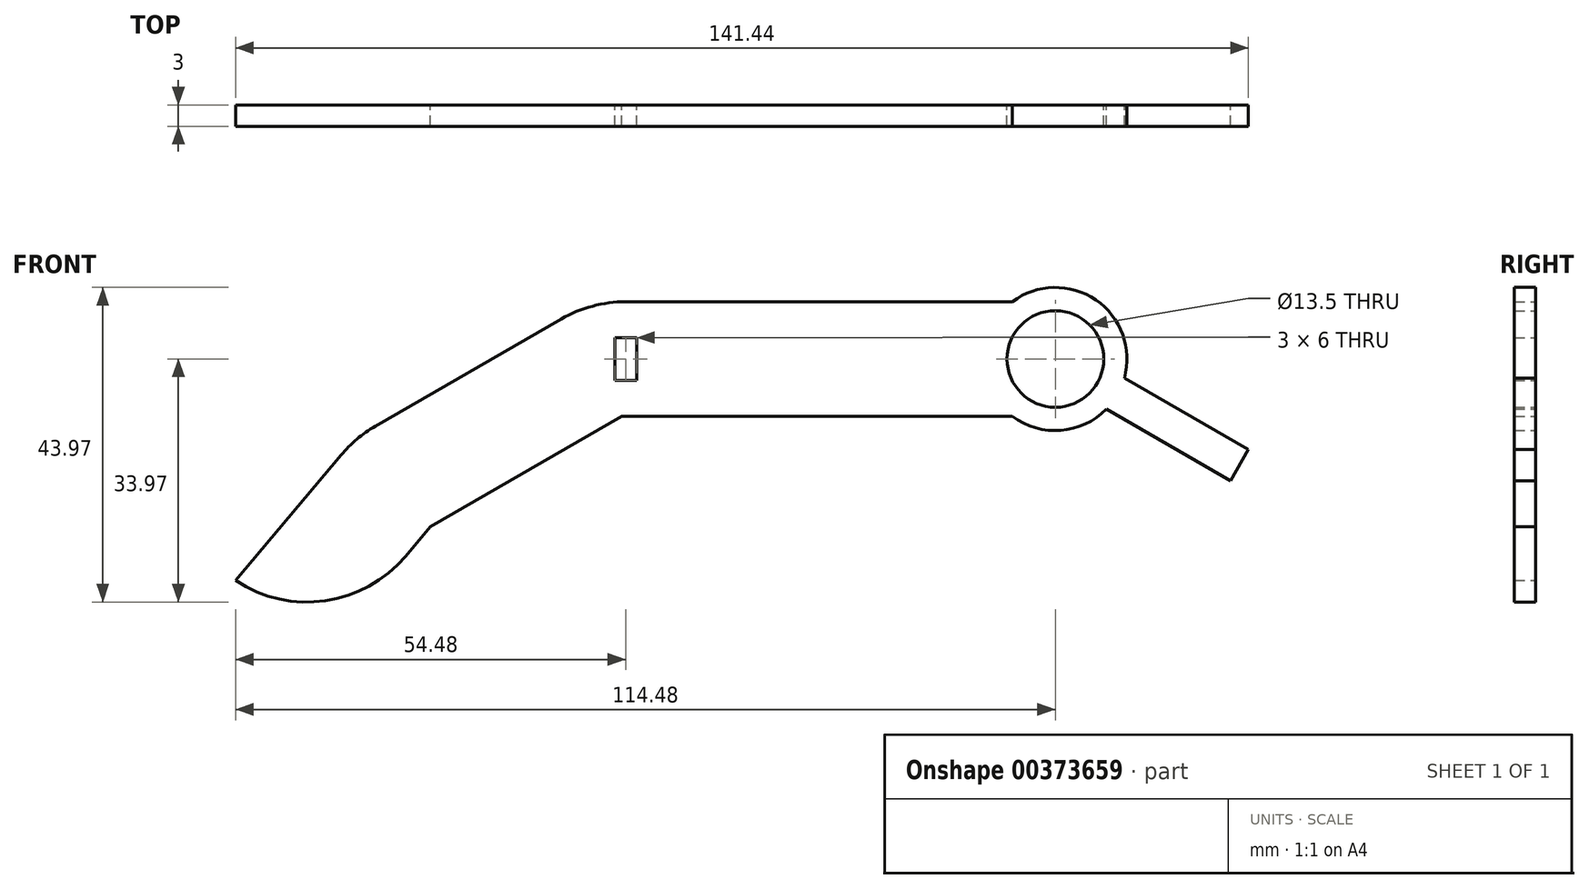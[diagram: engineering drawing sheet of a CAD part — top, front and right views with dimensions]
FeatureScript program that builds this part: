
annotation { "Feature Type Name" : "Feature", "Feature Type Description" : "" }
export const myFeature = defineFeature(function(context is Context, id is Id, definition is map)
    precondition{}
    {
        {
            var Q0;
            Q0=qCreatedBy(makeId("Front.planeOp"),FACE);
            var sketch = newSketch(context, id + "F0", { "sketchPlane" : qUnion([Q0])});
            skLineSegment(sketch, "E0.bottom", {"start": v(30, -10) * mm, "end": v(-30, -10) * mm, "construction": true});
            skLineSegment(sketch, "E0.top", {"start": v(30, 10) * mm, "end": v(-30, 10) * mm, "construction": true});
            skLineSegment(sketch, "E0.left", {"start": v(30, -10) * mm, "end": v(30, 10) * mm, "construction": true});
            skLineSegment(sketch, "E0.right", {"start": v(-30, -10) * mm, "end": v(-30, 10) * mm, "construction": true});
            skPoint(sketch, "E0.middle", {"position": v(0, 0) * mm});
            skArc(sketch, "E1", {"start": v(-30, 10) * mm, "mid": v(-35.18, 9.32) * mm, "end": v(-40, 7.32) * mm, "construction": true});
            skLineSegment(sketch, "E2", {"start": v(-40, 7.32) * mm, "end": v(-30, -10) * mm, "construction": true});
            skLineSegment(sketch, "E3", {"start": v(-40, 7.32) * mm, "end": v(-65.98, -7.68) * mm, "construction": true});
            skLineSegment(sketch, "E4", {"start": v(-30, -10) * mm, "end": v(-55.98, -25) * mm, "construction": true});
            skLineSegment(sketch, "E5", {"start": v(-65.98, -7.68) * mm, "end": v(-55.98, -25) * mm, "construction": true});
            skArc(sketch, "E6", {"start": v(-65.98, -7.68) * mm, "mid": v(-68.84, -9.68) * mm, "end": v(-71.3, -12.14) * mm, "construction": true});
            skLineSegment(sketch, "E7", {"start": v(-71.3, -12.14) * mm, "end": v(-55.98, -25) * mm, "construction": true});
            skLineSegment(sketch, "E8", {"start": v(-71.3, -12.14) * mm, "end": v(-87.37, -31.3) * mm, "construction": true});
            skLineSegment(sketch, "E9", {"start": v(-55.98, -25) * mm, "end": v(-59.2, -28.83) * mm, "construction": true});
            skArc(sketch, "E10", {"start": v(-87.37, -31.3) * mm, "mid": v(-72.77, -35.9) * mm, "end": v(-59.2, -28.83) * mm, "construction": true});
            skCircle(sketch, "E11", {"center": v(30, 0) * mm, "radius": 6.75 * mm});
            skLineSegment(sketch, "E12.0", {"start": v(30, -8) * mm, "end": v(-30.54, -8) * mm, "construction": true});
            skLineSegment(sketch, "E12.1", {"start": v(-30.54, -8) * mm, "end": v(-57.29, -23.44) * mm});
            skLineSegment(sketch, "E12.2", {"start": v(-57.29, -23.44) * mm, "end": v(-60.73, -27.54) * mm});
            skArc(sketch, "E12.3", {"start": v(-84.48, -30.96) * mm, "mid": v(-71.95, -33.8) * mm, "end": v(-60.73, -27.54) * mm});
            skLineSegment(sketch, "E12.4", {"start": v(-69.77, -13.43) * mm, "end": v(-84.48, -30.96) * mm});
            skLineSegment(sketch, "E12.5", {"start": v(30, 8) * mm, "end": v(-30, 8) * mm, "construction": true});
            skArc(sketch, "E12.6", {"start": v(-30, 8) * mm, "mid": v(-34.66, 7.39) * mm, "end": v(-39, 5.59) * mm});
            skLineSegment(sketch, "E12.7", {"start": v(-39, 5.59) * mm, "end": v(-64.98, -9.41) * mm});
            skArc(sketch, "E12.8", {"start": v(-64.98, -9.41) * mm, "mid": v(-67.55, -11.21) * mm, "end": v(-69.77, -13.43) * mm});
            skLineSegment(sketch, "E13", {"start": v(30, -8) * mm, "end": v(30, -10) * mm});
            skLineSegment(sketch, "E14", {"start": v(30, 8) * mm, "end": v(30, 10) * mm});
            skArc(sketch, "E15", {"start": v(30, 10) * mm, "mid": v(26.84, 9.49) * mm, "end": v(24, 8) * mm});
            skArc(sketch, "E16", {"start": v(30, -10) * mm, "mid": v(26.84, -9.49) * mm, "end": v(24, -8) * mm});
            skLineSegment(sketch, "E17", {"start": v(-30, 8) * mm, "end": v(24, 8) * mm});
            skLineSegment(sketch, "E18", {"start": v(24, -8) * mm, "end": v(-30.54, -8) * mm});
            skLineSegment(sketch, "E19", {"start": v(30, 0) * mm, "end": v(55.7, -14.84) * mm, "construction": true});
            skArc(sketch, "E20", {"start": v(30, 10) * mm, "mid": v(37.96, 6.05) * mm, "end": v(39.64, -2.68) * mm});
            skArc(sketch, "E21", {"start": v(30, -10) * mm, "mid": v(33.87, -9.22) * mm, "end": v(37.14, -7) * mm});
            skLineSegment(sketch, "E22", {"start": v(37.14, -7) * mm, "end": v(54.46, -17) * mm});
            skLineSegment(sketch, "E23", {"start": v(54.46, -17) * mm, "end": v(56.96, -12.68) * mm});
            skLineSegment(sketch, "E24", {"start": v(56.96, -12.68) * mm, "end": v(39.64, -2.68) * mm});
            skLineSegment(sketch, "E25.bottom", {"start": v(-28.5, -3) * mm, "end": v(-31.5, -3) * mm});
            skLineSegment(sketch, "E25.top", {"start": v(-28.5, 3) * mm, "end": v(-31.5, 3) * mm});
            skLineSegment(sketch, "E25.left", {"start": v(-28.5, -3) * mm, "end": v(-28.5, 3) * mm});
            skLineSegment(sketch, "E25.right", {"start": v(-31.5, -3) * mm, "end": v(-31.5, 3) * mm});
            skPoint(sketch, "E25.middle", {"position": v(-30, 0) * mm});
            skSolve(sketch);
        }
        {
            var Q0;
            Q0=qSketchRegion(id+"F0",true);
            extrude(context, id + "F1", {"entities" : qUnion([Q0]), "depth" : 3 * mm});
        }
    });
